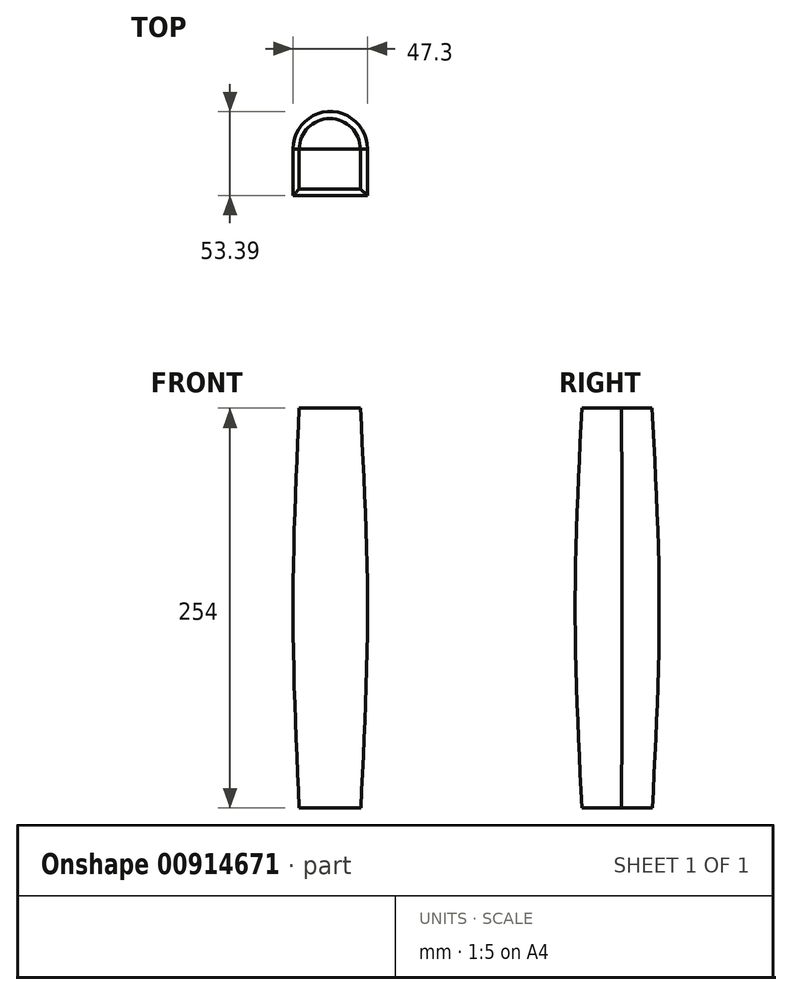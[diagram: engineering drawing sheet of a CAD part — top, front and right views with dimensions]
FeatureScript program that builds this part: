
annotation { "Feature Type Name" : "Feature", "Feature Type Description" : "" }
export const myFeature = defineFeature(function(context is Context, id is Id, definition is map)
    precondition{}
    {
        {
            var Q0;
            Q0=qCreatedBy(makeId("Top.planeOp"),FACE);
            var sketch = newSketch(context, id + "F0", { "sketchPlane" : qUnion([Q0])});
            skLineSegment(sketch, "E0.bottom", {"start": v(-18.55, -7.93) * mm, "end": v(20.53, -7.93) * mm});
            skLineSegment(sketch, "E0.top", {"start": v(-18.55, -33.14) * mm, "end": v(20.53, -33.14) * mm});
            skLineSegment(sketch, "E0.left", {"start": v(-18.55, -7.93) * mm, "end": v(-18.55, -33.14) * mm});
            skLineSegment(sketch, "E0.right", {"start": v(20.53, -7.93) * mm, "end": v(20.53, -33.14) * mm});
            skArc(sketch, "E1", {"start": v(20.53, -7.93) * mm, "mid": v(1, 11.61) * mm, "end": v(-18.55, -7.93) * mm});
            skSolve(sketch);
        }
        {
            var Q0;
            Q0=qCreatedBy(makeId("Top.planeOp"),FACE);
            cPlane(context, id + "F1", {"entities" : qUnion([Q0]), "cplaneType" : CPlaneType.OFFSET, "offset" : 127 * mm, "width" : 152.4 * mm, "height" : 152.4 * mm});
        }
        {
            var Q0;
            Q0=qCreatedBy(id+"F1.planeOp",FACE);
            var sketch = newSketch(context, id + "F2", { "sketchPlane" : qUnion([Q0])});
            skLineSegment(sketch, "E2.bottom", {"start": v(-22.52, -7.65) * mm, "end": v(24.78, -7.65) * mm});
            skLineSegment(sketch, "E2.top", {"start": v(-22.52, -37.39) * mm, "end": v(24.78, -37.39) * mm});
            skLineSegment(sketch, "E2.left", {"start": v(-22.52, -7.65) * mm, "end": v(-22.52, -37.39) * mm});
            skLineSegment(sketch, "E2.right", {"start": v(24.78, -7.65) * mm, "end": v(24.78, -37.39) * mm});
            skArc(sketch, "E3", {"start": v(24.78, -7.65) * mm, "mid": v(1.13, 16) * mm, "end": v(-22.52, -7.65) * mm});
            skSolve(sketch);
        }
        {
            var Q0;
            Q0=qCreatedBy(id+"F1.planeOp",FACE);
            cPlane(context, id + "F3", {"entities" : qUnion([Q0]), "cplaneType" : CPlaneType.OFFSET, "offset" : 127 * mm, "width" : 152.4 * mm, "height" : 152.4 * mm});
        }
        {
            var Q0;
            Q0=qCreatedBy(id+"F3.planeOp",FACE);
            var sketch = newSketch(context, id + "F4", { "sketchPlane" : qUnion([Q0])});
            skLineSegment(sketch, "E4.bottom", {"start": v(-18.55, -33.14) * mm, "end": v(20.25, -33.14) * mm});
            skLineSegment(sketch, "E4.top", {"start": v(-18.55, -7.93) * mm, "end": v(20.25, -7.93) * mm});
            skLineSegment(sketch, "E4.left", {"start": v(-18.55, -33.14) * mm, "end": v(-18.55, -7.93) * mm});
            skLineSegment(sketch, "E4.right", {"start": v(20.25, -33.14) * mm, "end": v(20.25, -7.93) * mm});
            skArc(sketch, "E5", {"start": v(20.25, -7.93) * mm, "mid": v(0.85, 11.47) * mm, "end": v(-18.55, -7.93) * mm});
            skSolve(sketch);
        }
        {
            var Q0;
            Q0=makeQuery(id+"F4.imprint","IMPRINT",FACE,{"disambiguationData":[TD([[makeQuery(id+"F4.imprint","IMPRINT",EDGE,{"derivedFrom":sQuery(id+"F4.wireOp",EDGE,"E4.bottom")}),1.0]])]});
            var Q1;
            Q1=makeQuery(id+"F2.imprint","IMPRINT",FACE,{"disambiguationData":[TD([[makeQuery(id+"F2.imprint","IMPRINT",EDGE,{"derivedFrom":sQuery(id+"F2.wireOp",EDGE,"E2.top")}),1.0]])]});
            var Q2;
            Q2=makeQuery(id+"F0.imprint","IMPRINT",FACE,{"disambiguationData":[TD([[makeQuery(id+"F0.imprint","IMPRINT",EDGE,{"derivedFrom":sQuery(id+"F0.wireOp",EDGE,"E0.top")}),1.0]])]});
            loft(context, id + "F5", {"sheetProfilesArray" : [{ "sheetProfileEntities" : qUnion([Q0]) }, { "sheetProfileEntities" : qUnion([Q1]) }, { "sheetProfileEntities" : qUnion([Q2]) }]});
        }
        {
            var Q0;
            Q0=makeQuery(id+"F4.imprint","IMPRINT",FACE,{"disambiguationData":[TD([[makeQuery(id+"F4.imprint","IMPRINT",EDGE,{"derivedFrom":sQuery(id+"F4.wireOp",EDGE,"E5")}),1.0]])]});
            var Q1;
            Q1=makeQuery(id+"F2.imprint","IMPRINT",FACE,{"disambiguationData":[TD([[makeQuery(id+"F2.imprint","IMPRINT",EDGE,{"derivedFrom":sQuery(id+"F2.wireOp",EDGE,"E3")}),1.0]])]});
            var Q2;
            Q2=makeQuery(id+"F0.imprint","IMPRINT",FACE,{"disambiguationData":[TD([[makeQuery(id+"F0.imprint","IMPRINT",EDGE,{"derivedFrom":sQuery(id+"F0.wireOp",EDGE,"E1")}),1.0]])]});
            loft(context, id + "F6", {"sheetProfilesArray" : [{ "sheetProfileEntities" : qUnion([Q0]) }, { "sheetProfileEntities" : qUnion([Q1]) }, { "sheetProfileEntities" : qUnion([Q2]) }]});
        }
    });
